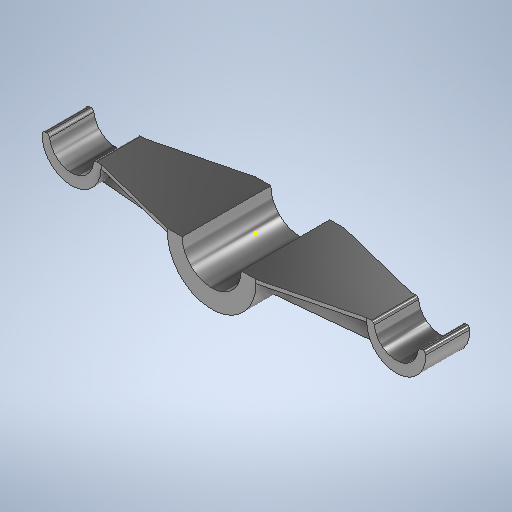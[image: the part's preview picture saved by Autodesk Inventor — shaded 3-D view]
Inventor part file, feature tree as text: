
AUTODESK INVENTOR PART (.ipt)
format: ipt  version: 2025.2 (Build 292293000, 293)  size: 461,824 bytes
history: native  units: in
note: dims shown in document units (in); Inventor stores cm internally (conversion verified against a paired STEP export)
features: sketch x7, extrude x3, mirror x2, rib x1, other x1
ambient origin geometry x8: Origin, YZ Plane, XZ Plane, XY Plane, X Axis, Y Axis, Z Axis, Center Point
bodies: Solid1 (feature_tree)
feature tree (14):
  extrude  "Extrusion1"  Depth=0.0984in
  sketch  "Sketch2"  dims[d7=0.7874in d10=2.3622in d11=0.0in]
  sketch  "Sketch3"  dims[d15=0.0984in d16=0.0in d18=0.7874in]
  sketch  "Sketch4"  dims[d20=0.5906in]
  extrude  "Extrusion2"  Depth=2.3622in TaperAngle=0.0deg
  extrude  "Extrusion3"  Depth=0.7874in
  mirror  "Mirror1"
  rib  "Rib1"
  mirror  "Mirror2"
  sketch  "Sketch1"  dims[d4=1.1811in d6=0.0984in]
  other  "Image1"
  sketch  "Sketch5"  dims[d21=0.0787in]
  sketch  "Sketch6"  dims[d22=1.1811in d23=0.0in]
  sketch  "Sketch7"  dims[d24=0.0394in d25=0.0984in d26=0.0in d27=0.0in d28=0.0394in d29=0.0394in d14=0.0197in d17=0.0344in]
